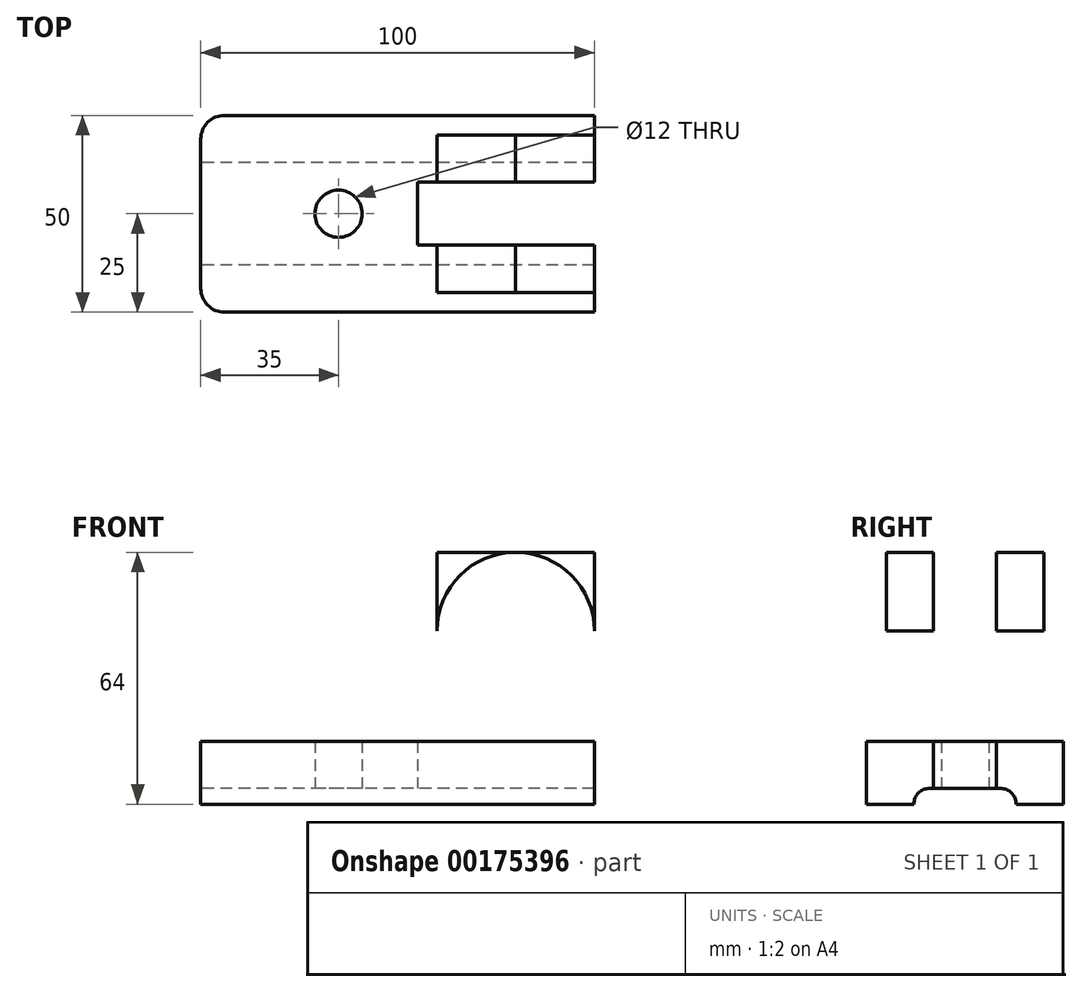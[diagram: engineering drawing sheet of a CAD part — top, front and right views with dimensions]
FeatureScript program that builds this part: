
annotation { "Feature Type Name" : "Feature", "Feature Type Description" : "" }
export const myFeature = defineFeature(function(context is Context, id is Id, definition is map)
    precondition{}
    {
        {
            var Q0;
            Q0=qCreatedBy(makeId("Top.planeOp"),FACE);
            var sketch = newSketch(context, id + "F0", { "sketchPlane" : qUnion([Q0])});
            skLineSegment(sketch, "E0.bottom", {"start": v(50, 25) * mm, "end": v(-44, 25) * mm});
            skLineSegment(sketch, "E0.top", {"start": v(50, -25) * mm, "end": v(-44, -25) * mm});
            skLineSegment(sketch, "E0.left", {"start": v(50, 25) * mm, "end": v(50, 8) * mm});
            skLineSegment(sketch, "E0.right", {"start": v(-50, 19) * mm, "end": v(-50, -19) * mm});
            skPoint(sketch, "E0.middle", {"position": v(0, 0) * mm});
            skLineSegment(sketch, "E1.bottom", {"start": v(50, 8) * mm, "end": v(5, 8) * mm});
            skLineSegment(sketch, "E1.top", {"start": v(50, -8) * mm, "end": v(5, -8) * mm});
            skLineSegment(sketch, "E1.right", {"start": v(5, 8) * mm, "end": v(5, -8) * mm});
            skLineSegment(sketch, "E2.trimOffspring", {"start": v(50, -8) * mm, "end": v(50, -25) * mm});
            skPoint(sketch, "E3.visualSharp", {"position": v(-50, 25) * mm});
            skArc(sketch, "E3.filletArc", {"start": v(-44, 25) * mm, "mid": v(-48.24, 23.24) * mm, "end": v(-50, 19) * mm});
            skPoint(sketch, "E4.visualSharp", {"position": v(-50, -25) * mm});
            skArc(sketch, "E4.filletArc", {"start": v(-50, -19) * mm, "mid": v(-48.24, -23.24) * mm, "end": v(-44, -25) * mm});
            skArc(sketch, "E5", {"start": v(-15, 20) * mm, "mid": v(-35, 0) * mm, "end": v(-15, -20) * mm});
            skLineSegment(sketch, "E6", {"start": v(-15, 20) * mm, "end": v(10, 20) * mm});
            skLineSegment(sketch, "E7", {"start": v(10, 20) * mm, "end": v(10, 8) * mm});
            skLineSegment(sketch, "E8.MirrorCS", {"start": v(-15, -20) * mm, "end": v(10, -20) * mm});
            skLineSegment(sketch, "E9.MirrorCS", {"start": v(10, -20) * mm, "end": v(10, -8) * mm});
            skCircle(sketch, "E10", {"center": v(-15, 0) * mm, "radius": 6 * mm});
            skLineSegment(sketch, "E11.bottom", {"start": v(10, 20) * mm, "end": v(50, 20) * mm});
            skLineSegment(sketch, "E11.top", {"start": v(10, 8) * mm, "end": v(50, 8) * mm});
            skLineSegment(sketch, "E11.right", {"start": v(50, 20) * mm, "end": v(50, 8) * mm});
            skLineSegment(sketch, "E12.MirrorCS", {"start": v(10, -20) * mm, "end": v(50, -20) * mm});
            skSolve(sketch);
        }
        {
            var Q0;
            Q0 = qSketchRegion(id + "F0", true);
            extrude(context, id + "F1", {"entities" : qUnion([Q0]), "depth" : 16 * mm});
        }
        {
            var Q0;
            Q0=makeQuery(id+"F0.imprint","IMPRINT",FACE,{"disambiguationData":[TD([[makeQuery(id+"F0.imprint","IMPRINT",EDGE,{"derivedFrom":sQuery(id+"F0.wireOp",EDGE,"E1.bottom")}),-1.0]])]});
            var Q1;
            {var subQ3=sQuery(id+"F0.wireOp",EDGE,"E9.MirrorCS");Q1=makeQuery(id+"F0.imprint","IMPRINT",FACE,{"disambiguationData":[TD([[makeQuery(id+"F0.imprint","IMPRINT",EDGE,{"derivedFrom":subQ3}),-1.0]])]});}
            var Q2;
            Q2=makeQuery(id+"F0.imprint","IMPRINT",FACE,{"disambiguationData":[TD([[makeQuery(id+"F0.imprint","IMPRINT",EDGE,{"derivedFrom":sQuery(id+"F0.wireOp",EDGE,"E11.bottom")}),-1.0]])]});
            extrude(context, id + "F2", {"entities" : qUnion([Q0, Q1, Q2]), "operationType" : NewBodyOperationType.ADD, "depth" : 24 * mm});
        }
        {
            var Q0;
            {var subQ3=sQuery(id+"F0.wireOp",EDGE,"E9.MirrorCS");Q0=makeQuery(id+"F0.imprint","IMPRINT",FACE,{"disambiguationData":[TD([[makeQuery(id+"F0.imprint","IMPRINT",EDGE,{"derivedFrom":subQ3}),-1.0]])]});}
            var Q1;
            Q1=makeQuery(id+"F0.imprint","IMPRINT",FACE,{"disambiguationData":[TD([[makeQuery(id+"F0.imprint","IMPRINT",EDGE,{"derivedFrom":sQuery(id+"F0.wireOp",EDGE,"E11.bottom")}),-1.0]])]});
            extrude(context, id + "F3", {"entities" : qUnion([Q0, Q1]), "operationType" : NewBodyOperationType.ADD, "depth" : 64 * mm});
        }
        {
            var Q0;
            Q0=makeQuery(id+"F1.opExtrude","SWEPT_FACE",FACE,{"disambiguationData":[OSD([sQuery(id+"F0.wireOp",EDGE,"E0.right")])]});
            var sketch = newSketch(context, id + "F4", { "sketchPlane" : qUnion([Q0])});
            skPoint(sketch, "E13.middle", {"position": v(0, 0) * mm});
            skLineSegment(sketch, "E14.bottom", {"start": v(13, 0) * mm, "end": v(-13, 0) * mm});
            skLineSegment(sketch, "E14.top", {"start": v(9, 4) * mm, "end": v(-9, 4) * mm});
            skLineSegment(sketch, "E14.left", {"start": v(13, 0) * mm, "end": v(13, 0) * mm});
            skLineSegment(sketch, "E14.right", {"start": v(-13, 0) * mm, "end": v(-13, 0) * mm});
            skPoint(sketch, "E14.middle", {"position": v(0, 2) * mm});
            skPoint(sketch, "E15.visualSharp", {"position": v(-13, 4) * mm});
            skArc(sketch, "E15.filletArc", {"start": v(-9, 4) * mm, "mid": v(-11.83, 2.83) * mm, "end": v(-13, 0) * mm});
            skPoint(sketch, "E16.visualSharp", {"position": v(13, 4) * mm});
            skArc(sketch, "E16.filletArc", {"start": v(13, 0) * mm, "mid": v(11.83, 2.83) * mm, "end": v(9, 4) * mm});
            skSolve(sketch);
        }
        {
            var Q0;
            Q0 = qSketchRegion(id + "F4", true);
            extrude(context, id + "F5", {"entities" : qUnion([Q0]), "operationType" : NewBodyOperationType.REMOVE, "endBound" : BoundingType.THROUGH_ALL, "oppositeDirection" : true, "depth" : 25 * mm});
        }
        {
            var Q0;
            {var subQ0=sQuery(id+"F0.wireOp",EDGE,"E12.MirrorCS");Q0=makeQuery(id+"F3.boolean.opBoolean","MERGE",FACE,{"derivedFrom":[makeQuery(id+"F2.opExtrude","SWEPT_FACE",FACE,{"disambiguationData":[OSD([sQuery(id+"F0.wireOp",EDGE,"E8.MirrorCS"),subQ0])]}),makeQuery(id+"F3.opExtrude","SWEPT_FACE",FACE,{"disambiguationData":[OSD([subQ0])]})]});}
            var sketch = newSketch(context, id + "F6", { "sketchPlane" : qUnion([Q0])});
            skCircle(sketch, "E17", {"center": v(30, 44) * mm, "radius": 6.5 * mm});
            skPoint(sketch, "E17.centerSnap0", {"position": v(30, 64) * mm});
            skArc(sketch, "E18", {"start": v(10, 44) * mm, "mid": v(30, 64) * mm, "end": v(50, 44) * mm});
            skSolve(sketch);
        }
        {
            var Q0;
            Q0 = qSketchRegion(id + "F6", true);
            var Q1;
            {var subQ0=sQuery(id+"F6.wireOp",EDGE,"E18");var subQ1=sQuery(id+"F0.wireOp",EDGE,"E12.MirrorCS");var subQ4=makeQuery(id+"F3.opExtrude","CAP_EDGE",EDGE,{"disambiguationData":[OSD([subQ1])],"isStart":false});var subQ5=makeQuery(id+"F6.imprint","INTERSECT",VERTEX,{"derivedFrom":[subQ4,subQ0]});Q1=makeQuery(id+"F6.imprint","IMPRINT",FACE,{"disambiguationData":[TD([[makeQuery(id+"F6.imprint","IMPRINT",EDGE,{"disambiguationData":[TD([[subQ5,1.0]])],"derivedFrom":subQ0}),1.0]])]});}
            var Q2;
            {var subQ0=sQuery(id+"F6.wireOp",EDGE,"E18");var subQ1=sQuery(id+"F0.wireOp",EDGE,"E12.MirrorCS");var subQ5=makeQuery(id+"F3.opExtrude","CAP_EDGE",EDGE,{"disambiguationData":[OSD([subQ1])],"isStart":false});var subQ6=makeQuery(id+"F6.imprint","INTERSECT",VERTEX,{"derivedFrom":[subQ5,subQ0]});Q2=makeQuery(id+"F6.imprint","IMPRINT",FACE,{"disambiguationData":[TD([[makeQuery(id+"F6.imprint","IMPRINT",EDGE,{"disambiguationData":[TD([[subQ6,-1.0]])],"derivedFrom":subQ0}),1.0]])]});}
            extrude(context, id + "F7", {"entities" : qUnion([Q0, Q1, Q2]), "operationType" : NewBodyOperationType.REMOVE, "endBound" : BoundingType.THROUGH_ALL, "oppositeDirection" : true, "depth" : 25 * mm});
        }
    });
